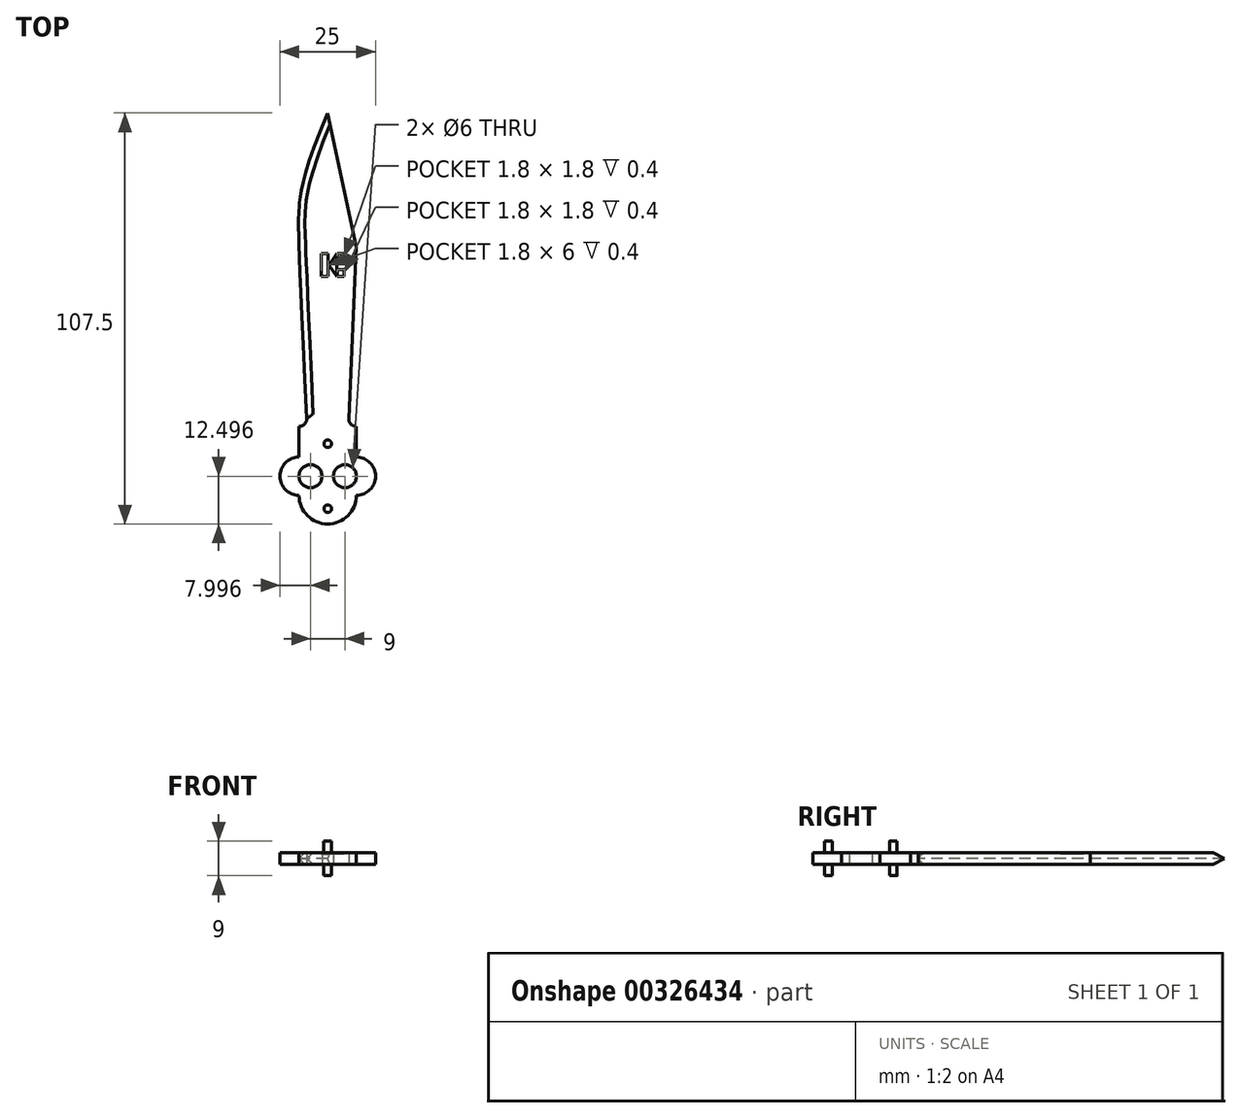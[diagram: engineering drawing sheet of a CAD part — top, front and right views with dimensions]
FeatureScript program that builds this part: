
annotation { "Feature Type Name" : "Feature", "Feature Type Description" : "" }
export const myFeature = defineFeature(function(context is Context, id is Id, definition is map)
    precondition{}
    {
        {
            var Q0;
            Q0=qCreatedBy(makeId("Top.planeOp"),FACE);
            var sketch = newSketch(context, id + "F0", { "sketchPlane" : qUnion([Q0])});
            skLineSegment(sketch, "E0.right", {"start": v(-33.18, -19.61) * mm, "end": v(-33.18, -27.61) * mm});
            skPoint(sketch, "E1", {"position": v(-33.18, 27.39) * mm});
            skPoint(sketch, "E2", {"position": v(-40.68, 62.39) * mm});
            skPoint(sketch, "E3", {"position": v(-48.18, -17.61) * mm});
            skLineSegment(sketch, "E4", {"start": v(-40.68, 62.39) * mm, "end": v(-33.18, 27.39) * mm});
            skArc(sketch, "E5", {"start": v(-35.18, -17.61) * mm, "mid": v(-34.6, -19.03) * mm, "end": v(-33.18, -19.61) * mm});
            skArc(sketch, "E6", {"start": v(-46.18, -17.61) * mm, "mid": v(-46.77, -19.03) * mm, "end": v(-48.18, -19.61) * mm});
            skLineSegment(sketch, "E7", {"start": v(-33.18, 27.39) * mm, "end": v(-35.18, -17.61) * mm});
            skLineSegment(sketch, "E8.trimOffspring", {"start": v(-48.18, -19.61) * mm, "end": v(-48.18, -27.61) * mm});
            skPoint(sketch, "E9", {"position": v(-48.18, 37.39) * mm});
            skFitSpline(sketch, "E10", {"points": [v(-40.68, 62.39) * mm, v(-48.18, 37.39) * mm, v(-46.18, -17.61) * mm], "startDerivative": vector(-50.77, -118.48) * mm, "endDerivative": vector(11.83, -259.4) * mm});
            skPoint(sketch, "E11", {"position": v(-48.18, -27.61) * mm});
            skPoint(sketch, "E12", {"position": v(-48.18, -32.61) * mm});
            skArc(sketch, "E13", {"start": v(-48.18, -27.61) * mm, "mid": v(-53.18, -32.61) * mm, "end": v(-48.18, -37.61) * mm});
            skArc(sketch, "E14", {"start": v(-33.18, -27.61) * mm, "mid": v(-28.18, -32.61) * mm, "end": v(-33.18, -37.61) * mm});
            skPoint(sketch, "E15", {"position": v(-45.18, -32.61) * mm});
            skPoint(sketch, "E16", {"position": v(-36.18, -32.61) * mm});
            skCircle(sketch, "E17", {"center": v(-45.18, -32.61) * mm, "radius": 3 * mm});
            skCircle(sketch, "E18", {"center": v(-36.18, -32.61) * mm, "radius": 3 * mm});
            skPoint(sketch, "E19", {"position": v(-40.68, -37.61) * mm});
            skArc(sketch, "E20", {"start": v(-48.18, -37.61) * mm, "mid": v(-40.68, -45.11) * mm, "end": v(-33.18, -37.61) * mm});
            skPoint(sketch, "E21", {"position": v(-40.68, -45.11) * mm});
            skSolve(sketch);
        }
        {
            var Q0;
            Q0=makeQuery(id+"F0.imprint","IMPRINT",FACE,{"disambiguationData":[TD([[makeQuery(id+"F0.imprint","IMPRINT",EDGE,{"derivedFrom":sQuery(id+"F0.wireOp",EDGE,"E0.right")}),-1.0]])]});
            extrude(context, id + "F1", {"entities" : qUnion([Q0]), "depth" : 3 * mm});
        }
        {
            var Q0;
            Q0=makeQuery(id+"F1.opExtrude","CAP_FACE",FACE,{"disambiguationData":[OSD([sQuery(id+"F0.wireOp",EDGE,"E0.right"),sQuery(id+"F0.wireOp",EDGE,"E4"),sQuery(id+"F0.wireOp",EDGE,"E5"),sQuery(id+"F0.wireOp",EDGE,"E6"),sQuery(id+"F0.wireOp",EDGE,"E7"),sQuery(id+"F0.wireOp",EDGE,"E8.trimOffspring"),sQuery(id+"F0.wireOp",EDGE,"E10"),sQuery(id+"F0.wireOp",EDGE,"E13"),sQuery(id+"F0.wireOp",EDGE,"E14"),sQuery(id+"F0.wireOp",EDGE,"E17"),sQuery(id+"F0.wireOp",EDGE,"E18"),sQuery(id+"F0.wireOp",EDGE,"E20")])],"isStart":false});
            var sketch = newSketch(context, id + "F2", { "sketchPlane" : qUnion([Q0])});
            skPoint(sketch, "E22", {"position": v(-45.18, -32.61) * mm});
            skPoint(sketch, "E23", {"position": v(-36.18, -32.61) * mm});
            skPoint(sketch, "E24", {"position": v(-40.68, -45.11) * mm});
            skLineSegment(sketch, "E25", {"start": v(-40.68, -45.11) * mm, "end": v(-40.68, -24.11) * mm, "construction": true});
            skPoint(sketch, "E26", {"position": v(-40.68, -24.11) * mm});
            skPoint(sketch, "E27", {"position": v(-40.68, -41.11) * mm});
            skCircle(sketch, "E28", {"center": v(-40.68, -41.11) * mm, "radius": 1 * mm});
            skCircle(sketch, "E29", {"center": v(-40.68, -24.11) * mm, "radius": 1 * mm});
            skPoint(sketch, "E30", {"position": v(-39.68, -24.11) * mm});
            skPoint(sketch, "E31", {"position": v(-39.18, -32.61) * mm});
            skPoint(sketch, "E32", {"position": v(-42.18, -32.61) * mm});
            skPoint(sketch, "E33", {"position": v(-53.18, -32.61) * mm});
            skPoint(sketch, "E34", {"position": v(-28.18, -32.61) * mm});
            skCircle(sketch, "E35", {"center": v(-40.68, -41.11) * mm, "radius": 1.5 * mm});
            skCircle(sketch, "E36", {"center": v(-40.68, -24.11) * mm, "radius": 1.5 * mm});
            skSolve(sketch);
        }
        {
            var Q0;
            Q0=makeQuery(id+"F2.imprint","IMPRINT",FACE,{"disambiguationData":[TD([[makeQuery(id+"F2.imprint","IMPRINT",EDGE,{"derivedFrom":sQuery(id+"F2.wireOp",EDGE,"E29")}),1.0]])]});
            var Q1;
            Q1=makeQuery(id+"F2.imprint","IMPRINT",FACE,{"disambiguationData":[TD([[makeQuery(id+"F2.imprint","IMPRINT",EDGE,{"derivedFrom":sQuery(id+"F2.wireOp",EDGE,"E28")}),1.0]])]});
            extrude(context, id + "F3", {"entities" : qUnion([Q0, Q1]), "operationType" : NewBodyOperationType.ADD, "depth" : 3 * mm});
        }
        {
            var Q0;
            Q0=makeQuery(id+"F3.opExtrude","CAP_FACE",FACE,{"disambiguationData":[OSD([sQuery(id+"F2.wireOp",EDGE,"E29")])],"isStart":false});
            var Q1;
            Q1=makeQuery(id+"F3.opExtrude","CAP_FACE",FACE,{"disambiguationData":[OSD([sQuery(id+"F2.wireOp",EDGE,"E28")])],"isStart":false});
            extrude(context, id + "F4", {"entities" : qUnion([Q0, Q1]), "operationType" : NewBodyOperationType.ADD, "oppositeDirection" : true, "depth" : 9 * mm});
        }
        {
            var Q0;
            Q0=makeQuery(id+"F1.opExtrude","SWEPT_FACE",FACE,{"disambiguationData":[OSD([sQuery(id+"F0.wireOp",EDGE,"E4")])]});
            var sketch = newSketch(context, id + "F5", { "sketchPlane" : qUnion([Q0])});
            skPoint(sketch, "E37", {"position": v(69.53, 1.5) * mm});
            skPoint(sketch, "E38", {"position": v(66.53, 3) * mm});
            skPoint(sketch, "E39", {"position": v(66.53, 0) * mm});
            skLineSegment(sketch, "E40", {"start": v(66.53, 3) * mm, "end": v(69.53, 1.5) * mm});
            skLineSegment(sketch, "E41", {"start": v(66.53, 0) * mm, "end": v(69.53, 1.5) * mm});
            skSolve(sketch);
        }
        {
            var Q0;
            {var subQ0=sQuery(id+"F5.wireOp",EDGE,"E41");Q0=makeQuery(id+"F5.imprint","IMPRINT",FACE,{"disambiguationData":[TD([[makeQuery(id+"F5.imprint","IMPRINT",EDGE,{"derivedFrom":subQ0}),-1.0]])]});}
            var Q1;
            {var subQ0=sQuery(id+"F5.wireOp",EDGE,"E40");Q1=makeQuery(id+"F5.imprint","IMPRINT",FACE,{"disambiguationData":[TD([[makeQuery(id+"F5.imprint","IMPRINT",EDGE,{"derivedFrom":subQ0}),1.0]])]});}
            var Q2;
            Q2=makeQuery(id+"F1.opExtrude","CAP_EDGE",EDGE,{"disambiguationData":[OSD([sQuery(id+"F0.wireOp",EDGE,"E10")])],"isStart":false});
            sweep(context, id + "F6", {"operationType" : NewBodyOperationType.REMOVE, "profiles" : qUnion([Q0, Q1]), "path" : qUnion([Q2])});
        }
        {
            var Q0;
            Q0=makeQuery(id+"F6.boolean.opBoolean","COPY",FACE,{"derivedFrom":makeQuery(id+"F6.opSweep","CAP_FACE",FACE,{"disambiguationData":[OSD([sQuery(id+"F0.wireOp",EDGE,"E4"),sQuery(id+"F0.wireOp",EDGE,"E6"),sQuery(id+"F0.wireOp",EDGE,"E10"),sQuery(id+"F5.wireOp",EDGE,"E40")])],"isStart":false})});
            var Q1;
            Q1=makeQuery(id+"F6.boolean.opBoolean","COPY",FACE,{"derivedFrom":makeQuery(id+"F6.opSweep","CAP_FACE",FACE,{"disambiguationData":[OSD([sQuery(id+"F0.wireOp",EDGE,"E4"),sQuery(id+"F0.wireOp",EDGE,"E6"),sQuery(id+"F0.wireOp",EDGE,"E10"),sQuery(id+"F5.wireOp",EDGE,"E41")])],"isStart":false})});
            extrude(context, id + "F7", {"entities" : qUnion([Q0, Q1]), "operationType" : NewBodyOperationType.ADD, "depth" : 3 * mm});
        }
        {
            var Q0;
            {var subQ0=sQuery(id+"F0.wireOp",EDGE,"E4");var subQ1=makeQuery(id+"F1.opExtrude","CAP_EDGE",EDGE,{"disambiguationData":[OSD([subQ0])],"isStart":false});var subQ2=sQuery(id+"F0.wireOp",EDGE,"E10");var subQ3=sQuery(id+"F0.wireOp",EDGE,"E6");Q0=makeQuery(id+"F7.boolean.opBoolean","MERGE",FACE,{"derivedFrom":[makeQuery(id+"F1.opExtrude","CAP_FACE",FACE,{"disambiguationData":[OSD([sQuery(id+"F0.wireOp",EDGE,"E0.right"),subQ0,sQuery(id+"F0.wireOp",EDGE,"E5"),subQ3,sQuery(id+"F0.wireOp",EDGE,"E7"),sQuery(id+"F0.wireOp",EDGE,"E8.trimOffspring"),subQ2,sQuery(id+"F0.wireOp",EDGE,"E13"),sQuery(id+"F0.wireOp",EDGE,"E14"),sQuery(id+"F0.wireOp",EDGE,"E17"),sQuery(id+"F0.wireOp",EDGE,"E18"),sQuery(id+"F0.wireOp",EDGE,"E20")])],"isStart":false}),makeQuery(id+"F7.opExtrude","SWEPT_FACE",FACE,{"disambiguationData":[OSD([subQ0,subQ3,subQ2]),TDD([makeQuery(id+"F6.boolean.opBoolean","COPY",EDGE,{"derivedFrom":makeQuery(id+"F6.opSweep","CAP_EDGE",EDGE,{"disambiguationData":[OSD([subQ0,subQ3,subQ2]),TDD([makeQuery(id+"F1.opExtrude","CAP_VERTEX",VERTEX,{"disambiguationData":[OSD([subQ3,subQ2])],"isStart":false}),makeQuery(id+"F5.imprint","IMPRINT",EDGE,{"disambiguationData":[TD([[makeQuery(id+"F5.imprint","INTERSECT",VERTEX,{"derivedFrom":[subQ1,sQuery(id+"F5.wireOp",EDGE,"E40")]}),1.0]])],"derivedFrom":subQ1})])],"isStart":false})})])]})]});}
            var sketch = newSketch(context, id + "F8", { "sketchPlane" : qUnion([Q0])});
            skLineSegment(sketch, "E42.bottom", {"start": v(-42.35, 25.6) * mm, "end": v(-40.55, 25.6) * mm});
            skLineSegment(sketch, "E42.top", {"start": v(-42.35, 19.6) * mm, "end": v(-40.55, 19.6) * mm});
            skLineSegment(sketch, "E42.left", {"start": v(-42.35, 25.6) * mm, "end": v(-42.35, 19.6) * mm});
            skLineSegment(sketch, "E42.right", {"start": v(-36.35, 25.6) * mm, "end": v(-36.35, 23.8) * mm});
            skPoint(sketch, "E43", {"position": v(-40.35, 22.6) * mm});
            skPoint(sketch, "E44", {"position": v(-38.35, 25.6) * mm});
            skLineSegment(sketch, "E45", {"start": v(-38.35, 25.6) * mm, "end": v(-40.35, 22.6) * mm});
            skLineSegment(sketch, "E46", {"start": v(-38.35, 25.6) * mm, "end": v(-38.35, 19.6) * mm});
            skLineSegment(sketch, "E47", {"start": v(-40.35, 22.6) * mm, "end": v(-38.35, 19.6) * mm});
            skPoint(sketch, "E48", {"position": v(-38.15, 25.6) * mm});
            skLineSegment(sketch, "E49", {"start": v(-38.15, 25.6) * mm, "end": v(-38.15, 23.8) * mm});
            skPoint(sketch, "E50", {"position": v(-36.35, 23.8) * mm});
            skPoint(sketch, "E51", {"position": v(-36.35, 21.4) * mm});
            skLineSegment(sketch, "E52", {"start": v(-36.35, 23.8) * mm, "end": v(-38.15, 23.8) * mm});
            skLineSegment(sketch, "E53", {"start": v(-36.35, 21.4) * mm, "end": v(-38.15, 21.4) * mm});
            skLineSegment(sketch, "E54.trimOffspring", {"start": v(-38.15, 21.4) * mm, "end": v(-38.15, 19.6) * mm});
            skLineSegment(sketch, "E55.trimOffspring", {"start": v(-38.15, 25.6) * mm, "end": v(-36.35, 25.6) * mm});
            skLineSegment(sketch, "E56.trimOffspring", {"start": v(-38.15, 19.6) * mm, "end": v(-36.35, 19.6) * mm});
            skLineSegment(sketch, "E57.trimOffspring", {"start": v(-36.35, 21.4) * mm, "end": v(-36.35, 19.6) * mm});
            skPoint(sketch, "E58", {"position": v(-40.55, 25.6) * mm});
            skLineSegment(sketch, "E59", {"start": v(-40.55, 25.6) * mm, "end": v(-40.55, 19.6) * mm});
            skSolve(sketch);
        }
        {
            var Q0;
            Q0=makeQuery(id+"F8.imprint","IMPRINT",FACE,{"disambiguationData":[TD([[makeQuery(id+"F8.imprint","IMPRINT",EDGE,{"derivedFrom":sQuery(id+"F8.wireOp",EDGE,"E42.bottom")}),-1.0]])]});
            var Q1;
            Q1=makeQuery(id+"F8.imprint","IMPRINT",FACE,{"disambiguationData":[TD([[makeQuery(id+"F8.imprint","IMPRINT",EDGE,{"derivedFrom":sQuery(id+"F8.wireOp",EDGE,"E45")}),1.0]])]});
            var Q2;
            Q2=makeQuery(id+"F8.imprint","IMPRINT",FACE,{"disambiguationData":[TD([[makeQuery(id+"F8.imprint","IMPRINT",EDGE,{"derivedFrom":sQuery(id+"F8.wireOp",EDGE,"E42.right")}),-1.0]])]});
            var Q3;
            Q3=makeQuery(id+"F8.imprint","IMPRINT",FACE,{"disambiguationData":[TD([[makeQuery(id+"F8.imprint","IMPRINT",EDGE,{"derivedFrom":sQuery(id+"F8.wireOp",EDGE,"E53")}),1.0]])]});
            extrude(context, id + "F9", {"entities" : qUnion([Q0, Q1, Q2, Q3]), "operationType" : NewBodyOperationType.REMOVE, "oppositeDirection" : true, "depth" : 0.4 * mm});
        }
    });
